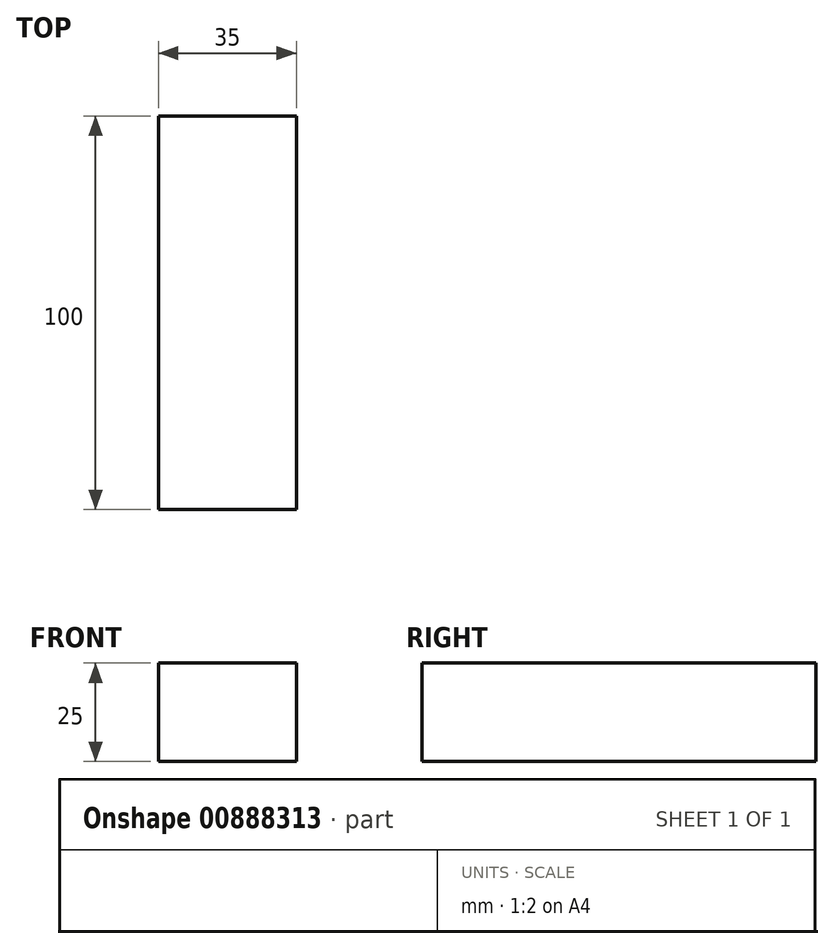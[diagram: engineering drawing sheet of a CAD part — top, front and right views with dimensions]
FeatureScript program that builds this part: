
annotation { "Feature Type Name" : "Feature", "Feature Type Description" : "" }
export const myFeature = defineFeature(function(context is Context, id is Id, definition is map)
    precondition{}
    {
        {
            var Q0;
            Q0=qCreatedBy(makeId("Top.planeOp"),FACE);
            var sketch = newSketch(context, id + "F0", { "sketchPlane" : qUnion([Q0])});
            skLineSegment(sketch, "E0.bottom", {"start": v(-17.5, 50) * mm, "end": v(17.5, 50) * mm});
            skLineSegment(sketch, "E0.top", {"start": v(-17.5, -50) * mm, "end": v(17.5, -50) * mm});
            skLineSegment(sketch, "E0.left", {"start": v(-17.5, 50) * mm, "end": v(-17.5, -50) * mm});
            skLineSegment(sketch, "E0.right", {"start": v(17.5, 50) * mm, "end": v(17.5, -50) * mm});
            skPoint(sketch, "E0.middle", {"position": v(0, 0) * mm});
            skSolve(sketch);
        }
        {
            var Q0;
            Q0 = qSketchRegion(id + "F0", true);
            extrude(context, id + "F1", {"entities" : qUnion([Q0]), "depth" : 25 * mm, "offsetDistance" : 25 * mm});
        }
    });
